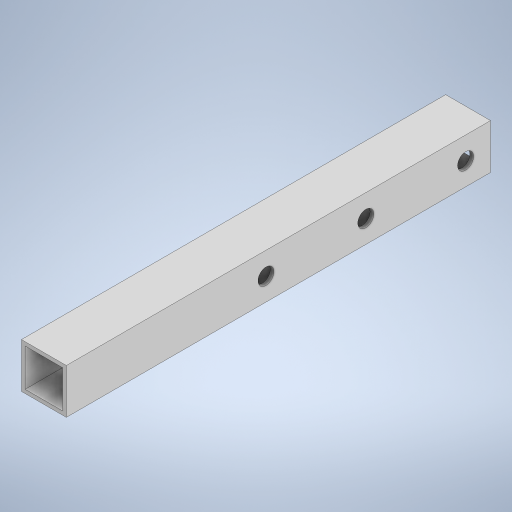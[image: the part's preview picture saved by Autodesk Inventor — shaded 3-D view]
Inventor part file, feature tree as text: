
AUTODESK INVENTOR PART (.ipt)
format: ipt  version: 2023 (Build 270158000, 158)  size: 248,832 bytes
history: native  units: mm
features: sketch x3, extrude x2, other x1, hole x1
ambient origin geometry x8: Origin, YZ Plane, XZ Plane, XY Plane, X Axis, Y Axis, Z Axis, Center Point
bodies: Body1 (feature_tree)
feature tree (7):
  other  "ソリッド1"
  extrude  "押し出し1"  Depth=9.0mm
  hole  "穴1"  [1 undecoded]
  extrude  "押し出し2"  Depth=7.5mm
  sketch  "スケッチ1"
  sketch  "スケッチ2"
  sketch  "スケッチ3"
note: 1 required parameter value undecoded (feature->parameter linkage not recoverable at this tier; creation-order binding heuristic only, values carry confidence <= 0.55)
